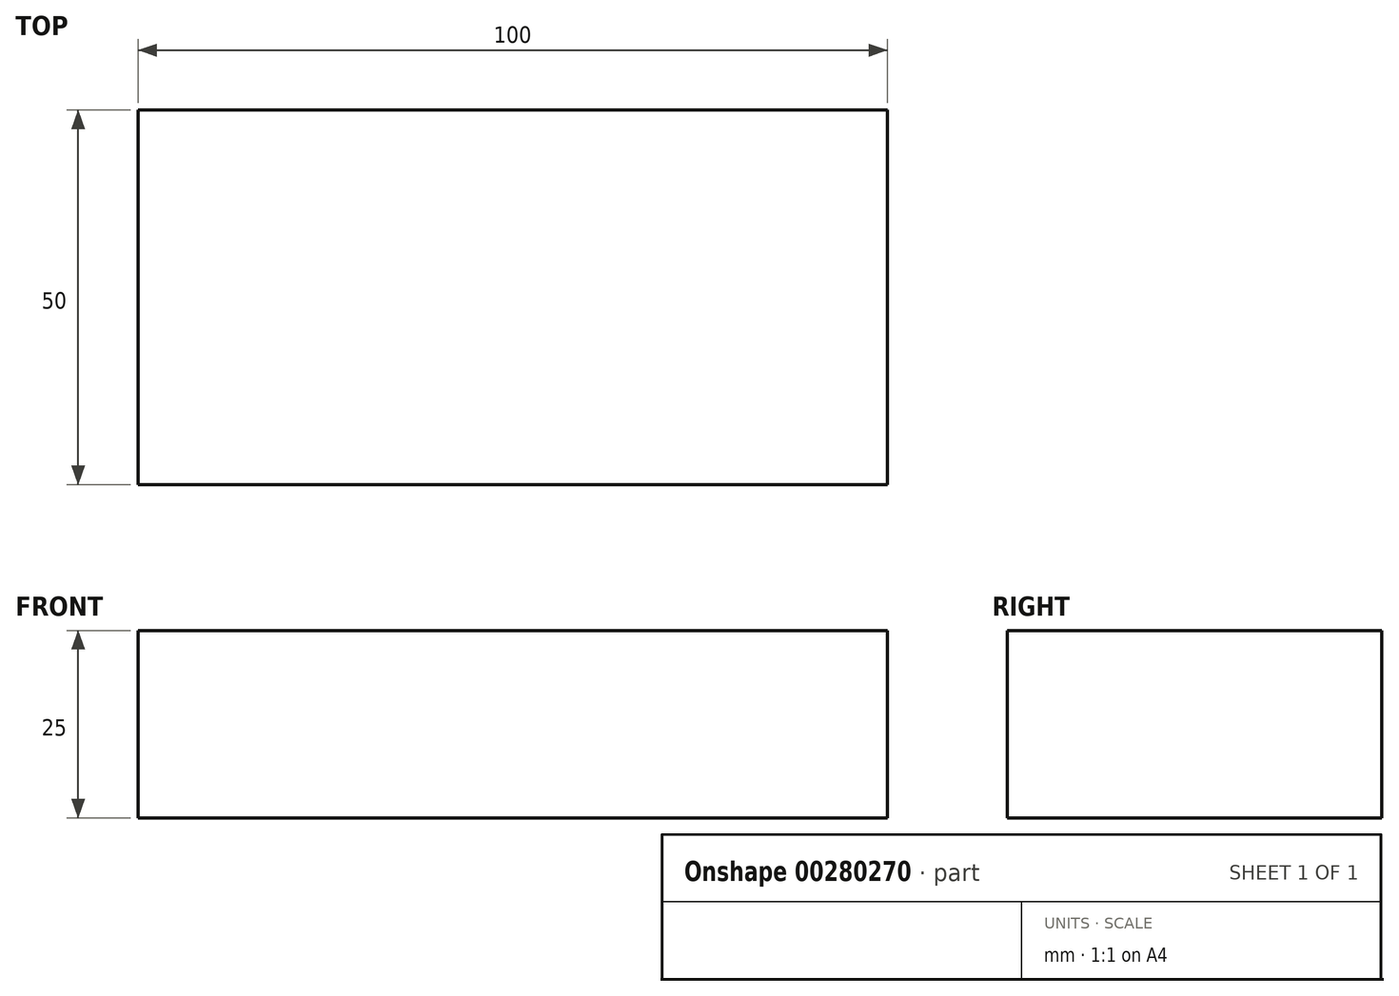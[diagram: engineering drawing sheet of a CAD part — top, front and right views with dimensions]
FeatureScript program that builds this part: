
annotation { "Feature Type Name" : "Feature", "Feature Type Description" : "" }
export const myFeature = defineFeature(function(context is Context, id is Id, definition is map)
    precondition{}
    {
        {
            var Q0;
            Q0=qCreatedBy(makeId("Top.planeOp"),FACE);
            var sketch = newSketch(context, id + "F0", { "sketchPlane" : qUnion([Q0])});
            skLineSegment(sketch, "E0.bottom", {"start": v(0, 0) * mm, "end": v(100, 0) * mm});
            skLineSegment(sketch, "E0.top", {"start": v(0, 50) * mm, "end": v(100, 50) * mm});
            skLineSegment(sketch, "E0.left", {"start": v(0, 0) * mm, "end": v(0, 50) * mm});
            skLineSegment(sketch, "E0.right", {"start": v(100, 0) * mm, "end": v(100, 50) * mm});
            skSolve(sketch);
        }
        {
            var Q0;
            Q0=makeQuery(id+"F0.imprint","IMPRINT",FACE,{"disambiguationData":[TD([[makeQuery(id+"F0.imprint","IMPRINT",EDGE,{"derivedFrom":sQuery(id+"F0.wireOp",EDGE,"E0.bottom")}),1.0]])]});
            extrude(context, id + "F1", {"entities" : qUnion([Q0]), "depth" : 25 * mm});
        }
    });
